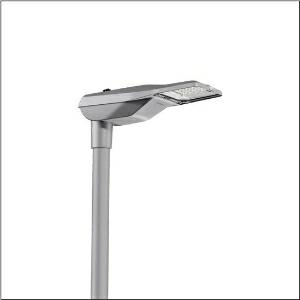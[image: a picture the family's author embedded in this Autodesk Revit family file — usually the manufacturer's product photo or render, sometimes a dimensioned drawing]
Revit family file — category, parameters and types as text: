
# Revit family: streetlight_sl_21_micro___stw1_0a_5xe1e33s08db_cbec
name_source: partatom
category: Lighting Fixtures
units: mm (PartAtom-declared; Revit-internal decimal feet)

## family parameters
Cut with Voids When Loaded = No
Host = Face
Light Source = No
Part Type = Normal
Room Calculation Point = No
Round Connector Dimension = Use Diameter
Shared = No

## types (1)
- --- (1 x LED, 5110 lm, 39.1 W, 3000K)
    Apparent Load = 39 VA
    CIE Flux Codes = 38 75 98 100 100
    Color Rendering = 70
    Color Temperature = 3000K
    Default Elevation = 1800 mm
    Description = Streetlight SL 21 micro, mast luminaire, primary light control with lens, of PMMA, primary optical cover: cover, of toughened safety glass, transparent, light distribution: STW1.0a, light emission: direct distribution, primary light characteristic: asymmetric, installation type: side-entry, post-top, LED, High Power LED, rated luminous flux: 5.110lm, luminous efficacy: 131lm/W, light colour: 730, colour temperature: 3000K, control gear: D4i, control: flexible luminous flux parameterisation, time-dependent luminous flux control, constant luminous flux control, overheat protection, pre-setting: logarithmic dimming characteristic, mains connection: 220..240V, AC, 50/60Hz, start of lifetime: 39W, end of service life: 41W, reduction: 18W, luminaire housing, of diecast aluminium, powder-coated, Siteco® metallic grey (DB 702S), corrosivity category C5 mid according to DIN EN ISO 12944, please order mast flange separately, inclination adjustable: 0°, 5°, 10°, 15°, sealing non-destructively replaceable, multi-level sealing system, length: 528mm, width: 235mm, height: 110mm, mast flange for spigot size: 42mm (side-entry): 5XC10008XM4, 60/48mm (side-entry/post-top): 5XC10108XM2, 76/60mm (side-entry/post-top): 5XC10108XM1, Smart Interface above, protection rating (complete): IP66, insulation class (complete): insulation class II (safety insulation), certification: CE, ENEC, ENEC+, VDE, impact resistance: IK10, permissible operating ambient temperature for outdoor applications: -40..+50°C, standard-compliant lighting for roads and squares, packaging unit: 1 piece

Light Distribution: STW1.0a
    Height = 110 mm
    Lamp = 1 x LED
    Lamp Light Flux = 5110 lm
    Lamp Power = 39.1 W
    Lamp count = 1
    Length = 528 mm
    Luminous efficacy = 131 lm/W
    Manufacturer = Siteco
    ModVariant = No
    Model = 5XE1E33S08DB
    Number of Poles = 1
    OnlyDefault = Yes
    Power Factor = 1
    Product Name = Streetlight SL 21 micro | STW1.0a
    Product group = mast luminaire | pylon top
    ProductGroupID = 6100
    Protection Class = Protection class II
    Protection Degree = IP 66
    RLX_Detail_Level = 1
    RLX_Emergency_Light_Flux = 0 lm
    RLX_Emergency_Type = 0
    RLX_Emergency_Type_DB = No
    RlxData = <blob elided: 98669 chars, md5=6e6d6b0e>
    Socket = socket
    Standby Power = 0 W
    System Light Flux = 5110 lm
    System Power = 39 W
    Type Comments = factory setting: luminous flux: 100 % | dim-lin: 254 | 765 mA
    Type Image = l_1277292.jpg
    URL = http://relux.com
    VarID = @adj_155386
    Voltage = 0 V
    Weight = 0.00 kg
    Width = 235 mm

## geometry (parser evidence)
native form markers: Blend x4, Sweep x9
no freeform markers — native parametric forms only
